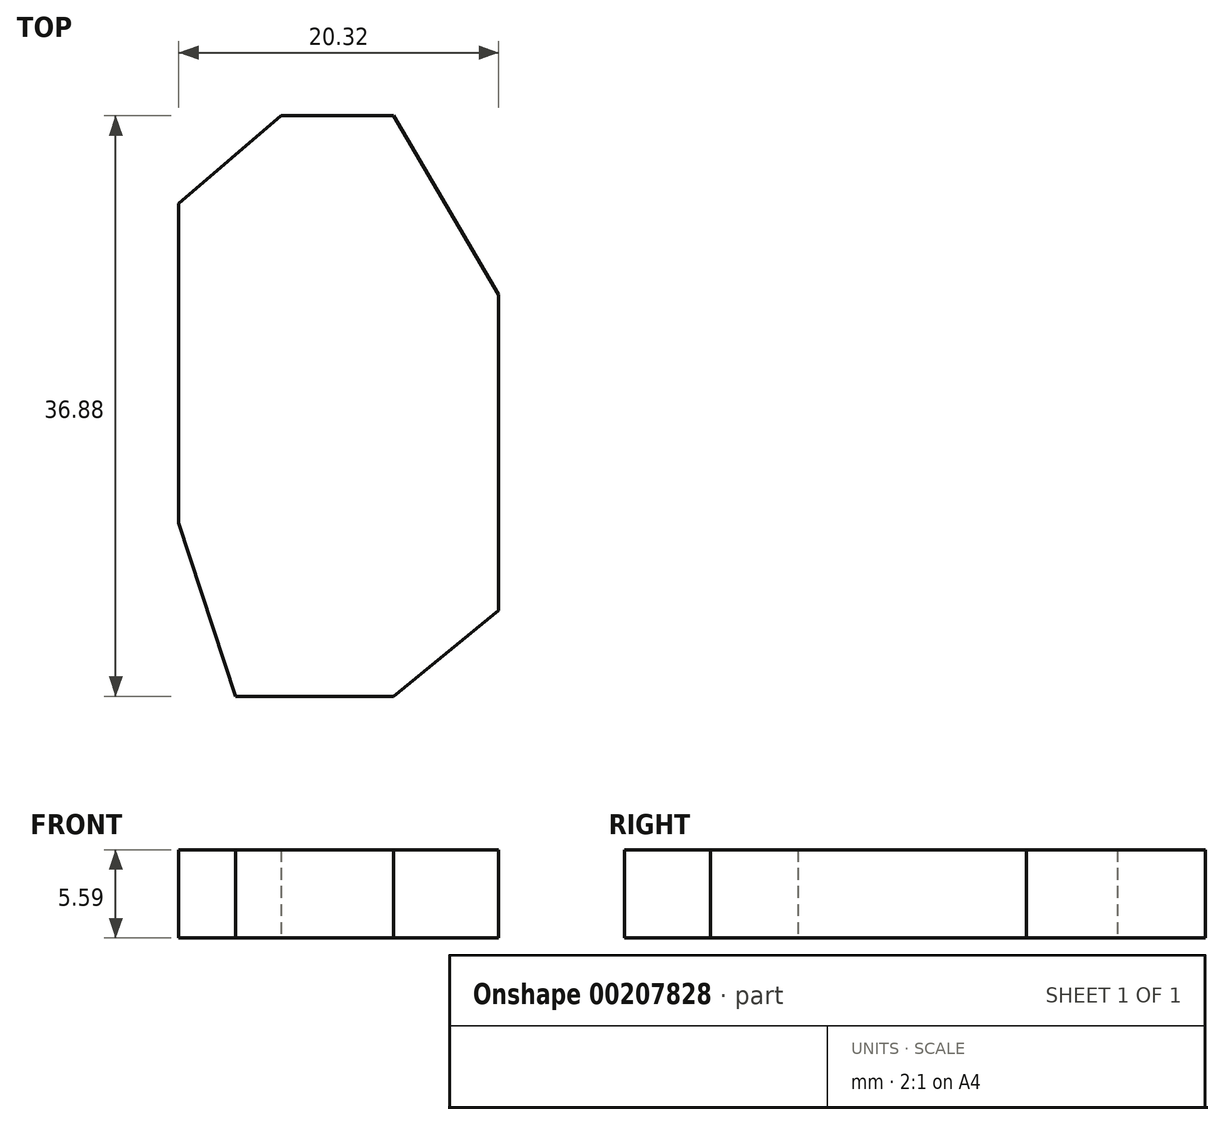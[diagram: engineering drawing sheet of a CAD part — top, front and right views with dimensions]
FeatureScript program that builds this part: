
annotation { "Feature Type Name" : "Feature", "Feature Type Description" : "" }
export const myFeature = defineFeature(function(context is Context, id is Id, definition is map)
    precondition{}
    {
        {
            var Q0;
            Q0=qCreatedBy(makeId("Top.planeOp"),FACE);
            var sketch = newSketch(context, id + "F0", { "sketchPlane" : qUnion([Q0])});
            skLineSegment(sketch, "E0", {"start": v(-37.54, -20.3) * mm, "end": v(-37.54, 0) * mm});
            skLineSegment(sketch, "E1", {"start": v(-37.54, 0) * mm, "end": v(-31.05, 5.58) * mm});
            skLineSegment(sketch, "E2", {"start": v(-31.05, 5.58) * mm, "end": v(-23.9, 5.58) * mm});
            skLineSegment(sketch, "E3", {"start": v(-23.9, 5.58) * mm, "end": v(-17.22, -5.8) * mm});
            skLineSegment(sketch, "E4", {"start": v(-17.22, -5.8) * mm, "end": v(-17.22, -25.84) * mm});
            skLineSegment(sketch, "E5", {"start": v(-17.22, -25.84) * mm, "end": v(-23.9, -31.3) * mm});
            skLineSegment(sketch, "E6", {"start": v(-33.93, -31.3) * mm, "end": v(-23.9, -31.3) * mm});
            skLineSegment(sketch, "E7", {"start": v(-33.93, -31.3) * mm, "end": v(-37.54, -20.3) * mm});
            skSolve(sketch);
        }
        {
            var Q0;
            Q0 = qSketchRegion(id + "F0", true);
            extrude(context, id + "F1", {"entities" : qUnion([Q0]), "depth" : 5.6 * mm});
        }
    });
